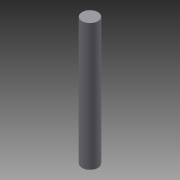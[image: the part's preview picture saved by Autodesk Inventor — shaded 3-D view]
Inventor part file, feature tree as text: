
AUTODESK INVENTOR PART (.ipt)
format: ipt  version: 2014 SP1 (Build 180222100, 222)  size: 64,000 bytes
history: native  units: in
note: dims shown in document units (in); Inventor stores cm internally (conversion verified against a paired STEP export)
features: extrude x1, sketch x1
ambient origin geometry x8: Origin, YZ Plane, XZ Plane, XY Plane, X Axis, Y Axis, Z Axis, Center Point
bodies: Solid1 (feature_tree)
feature tree (2):
  extrude  "Extrusion1"  Depth=3.0in TaperAngle=0.0deg
  sketch  "Sketch1"  dims[d0=0.375in d1=3.0in d2=0.0in]
